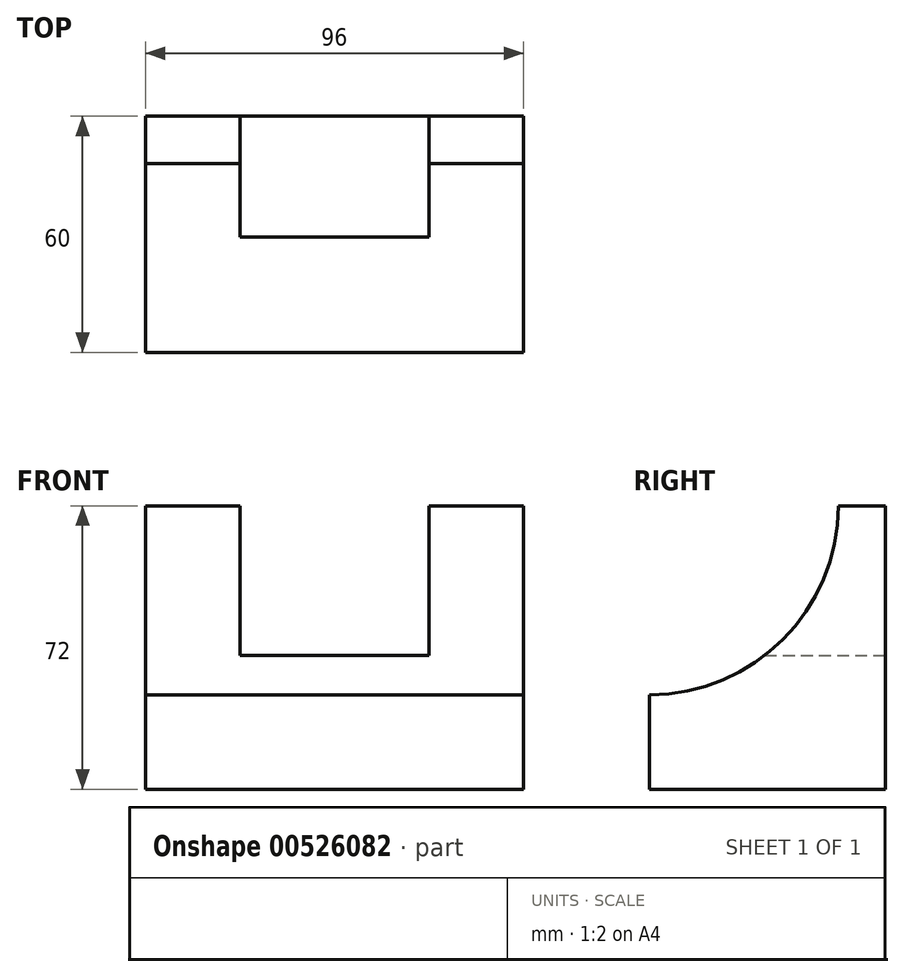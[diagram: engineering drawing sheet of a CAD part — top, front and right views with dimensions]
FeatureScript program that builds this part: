
annotation { "Feature Type Name" : "Feature", "Feature Type Description" : "" }
export const myFeature = defineFeature(function(context is Context, id is Id, definition is map)
    precondition{}
    {
        {
            var Q0;
            Q0=qCreatedBy(makeId("Right.planeOp"),FACE);
            var sketch = newSketch(context, id + "F0", { "sketchPlane" : qUnion([Q0])});
            skArc(sketch, "E0", {"start": v(0, -48) * mm, "mid": v(33.94, -33.94) * mm, "end": v(48, 0) * mm});
            skLineSegment(sketch, "E1.bottom", {"start": v(48, 0) * mm, "end": v(60, 0) * mm});
            skLineSegment(sketch, "E1.top", {"start": v(0, -72) * mm, "end": v(60, -72) * mm});
            skLineSegment(sketch, "E1.left", {"start": v(0, -48) * mm, "end": v(0, -72) * mm});
            skLineSegment(sketch, "E1.right", {"start": v(60, 0) * mm, "end": v(60, -72) * mm});
            skSolve(sketch);
        }
        {
            var Q0;
            Q0=makeQuery(id+"F0.imprint","IMPRINT",FACE,{"disambiguationData":[TD([[makeQuery(id+"F0.imprint","IMPRINT",EDGE,{"derivedFrom":sQuery(id+"F0.wireOp",EDGE,"E0")}),-1.0]])]});
            extrude(context, id + "F1", {"entities" : qUnion([Q0]), "endBound" : BoundingType.SYMMETRIC, "depth" : 96 * mm, "offsetDistance" : 25 * mm});
        }
        {
            var Q0;
            Q0=makeQuery(id+"F1.opExtrude","SWEPT_FACE",FACE,{"disambiguationData":[OSD([sQuery(id+"F0.wireOp",EDGE,"E1.right")])]});
            var sketch = newSketch(context, id + "F2", { "sketchPlane" : qUnion([Q0])});
            skLineSegment(sketch, "E2.bottom", {"start": v(-24, 0) * mm, "end": v(24, 0) * mm});
            skLineSegment(sketch, "E2.top", {"start": v(-24, -38) * mm, "end": v(24, -38) * mm});
            skLineSegment(sketch, "E2.left", {"start": v(-24, 0) * mm, "end": v(-24, -38) * mm});
            skLineSegment(sketch, "E2.right", {"start": v(24, 0) * mm, "end": v(24, -38) * mm});
            skLineSegment(sketch, "E3", {"start": v(0, -72) * mm, "end": v(0, 0) * mm, "construction": true});
            skSolve(sketch);
        }
        {
            var Q0;
            Q0=makeQuery(id+"F2.imprint","IMPRINT",FACE,{"disambiguationData":[TD([[makeQuery(id+"F2.imprint","IMPRINT",EDGE,{"derivedFrom":sQuery(id+"F2.wireOp",EDGE,"E2.bottom")}),-1.0]])]});
            extrude(context, id + "F3", {"entities" : qUnion([Q0]), "operationType" : NewBodyOperationType.REMOVE, "endBound" : BoundingType.THROUGH_ALL, "oppositeDirection" : true, "depth" : 25 * mm, "offsetDistance" : 25 * mm});
        }
    });
